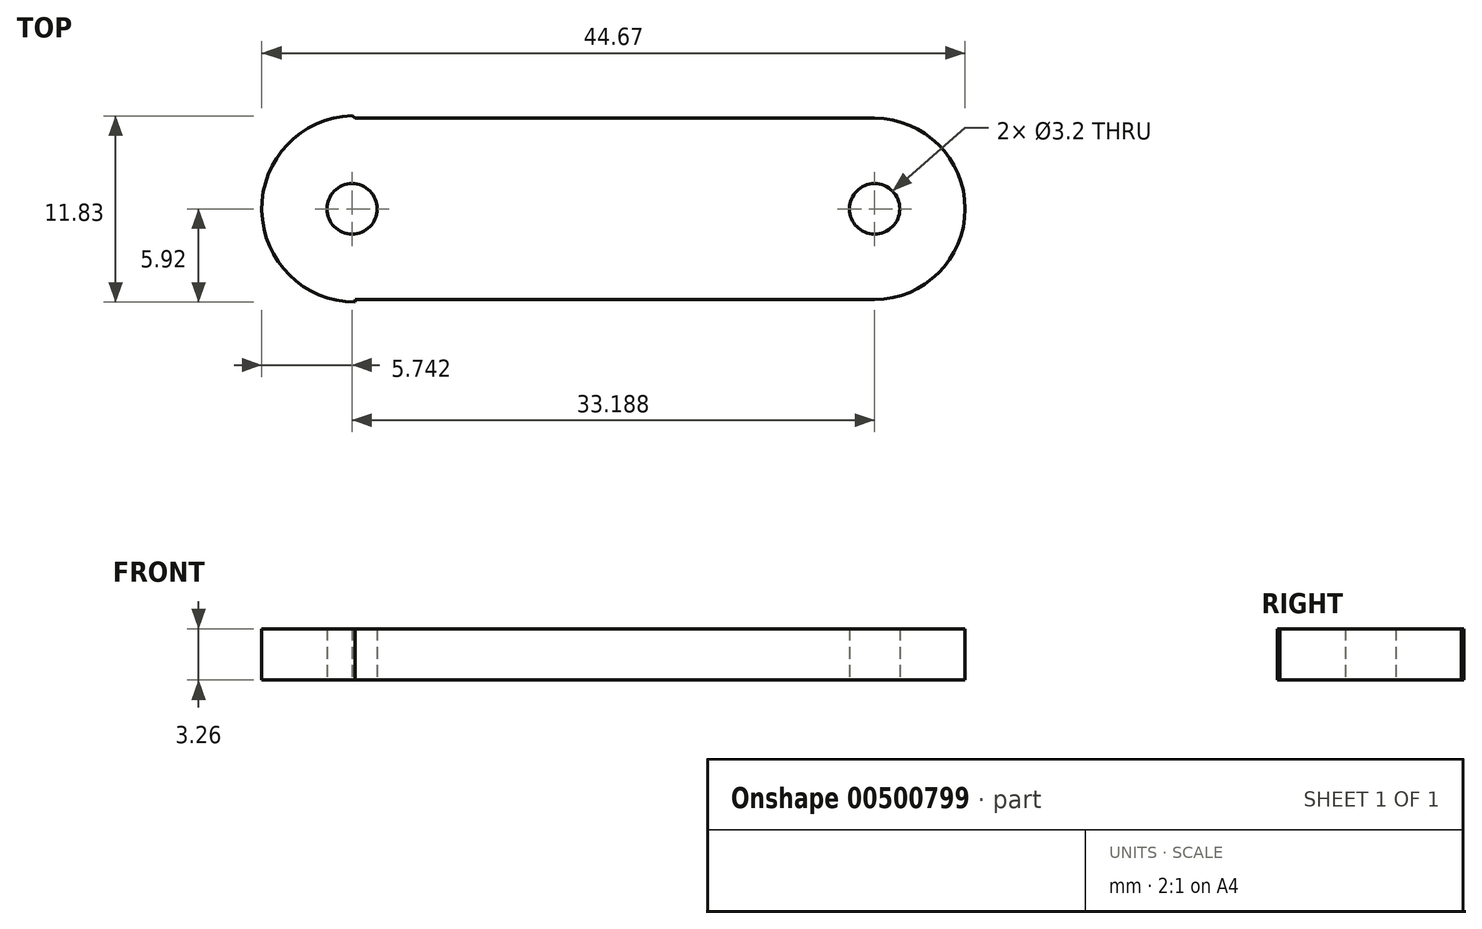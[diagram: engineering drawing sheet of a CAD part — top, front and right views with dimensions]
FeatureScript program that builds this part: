
annotation { "Feature Type Name" : "Feature", "Feature Type Description" : "" }
export const myFeature = defineFeature(function(context is Context, id is Id, definition is map)
    precondition{}
    {
        {
            var Q0;
            Q0=qCreatedBy(makeId("Top.planeOp"),FACE);
            var sketch = newSketch(context, id + "F0", { "sketchPlane" : qUnion([Q0])});
            skLineSegment(sketch, "E0.bottom", {"start": v(16.5, 5.75) * mm, "end": v(-16.5, 5.75) * mm});
            skLineSegment(sketch, "E0.top", {"start": v(16.5, -5.75) * mm, "end": v(-16.5, -5.75) * mm});
            skLineSegment(sketch, "E0.left", {"start": v(16.5, 5.75) * mm, "end": v(16.5, -5.75) * mm});
            skLineSegment(sketch, "E0.right", {"start": v(-16.5, 5.75) * mm, "end": v(-16.5, -5.75) * mm});
            skPoint(sketch, "E0.middle", {"position": v(0, 0) * mm});
            skArc(sketch, "E1", {"start": v(-22.42, 0) * mm, "mid": v(-20.75, 4.12) * mm, "end": v(-16.7, 5.91) * mm});
            skPoint(sketch, "E1.startSnap0", {"position": v(-16.5, 0) * mm});
            skArc(sketch, "E2", {"start": v(-22.42, 0) * mm, "mid": v(-20.68, -4.18) * mm, "end": v(-16.5, -5.92) * mm});
            skArc(sketch, "E3", {"start": v(22.25, 0) * mm, "mid": v(20.57, 4.07) * mm, "end": v(16.5, 5.75) * mm});
            skPoint(sketch, "E3.startSnap0", {"position": v(16.5, 0) * mm});
            skArc(sketch, "E4", {"start": v(22.25, 0) * mm, "mid": v(20.57, -4.07) * mm, "end": v(16.5, -5.75) * mm});
            skPoint(sketch, "E5", {"position": v(-16.68, 0) * mm});
            skCircle(sketch, "E6", {"center": v(-16.68, 0) * mm, "radius": 1.6 * mm});
            skPoint(sketch, "E7", {"position": v(16.51, 0) * mm});
            skCircle(sketch, "E8", {"center": v(16.51, 0) * mm, "radius": 1.6 * mm});
            skLineSegment(sketch, "E9", {"start": v(-16.5, 5.75) * mm, "end": v(-16.7, 5.91) * mm});
            skLineSegment(sketch, "E10", {"start": v(-16.5, -5.92) * mm, "end": v(-16.5, -5.75) * mm});
            skSolve(sketch);
        }
        {
            var Q0;
            Q0 = qSketchRegion(id + "F0", true);
            var Q1;
            {var subQ4=sQuery(id+"F0.wireOp",EDGE,"E0.bottom");Q1=makeQuery(id+"F0.imprint","IMPRINT",FACE,{"disambiguationData":[TD([[makeQuery(id+"F0.imprint","IMPRINT",EDGE,{"derivedFrom":subQ4}),1.0]])]});}
            extrude(context, id + "F1", {"entities" : qUnion([Q0, Q1]), "depth" : 3.25 * mm, "offsetDistance" : 25 * mm, "symmetric" : true});
        }
    });
